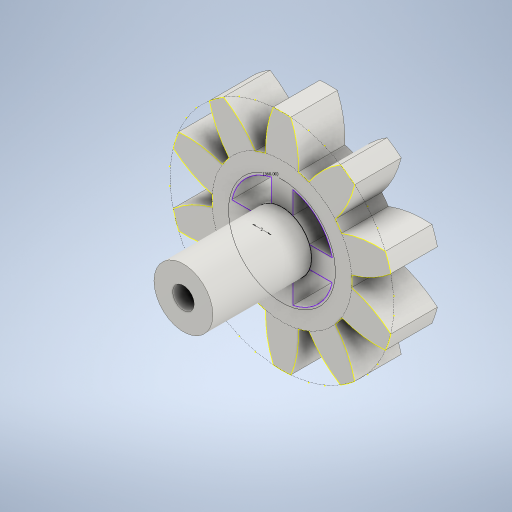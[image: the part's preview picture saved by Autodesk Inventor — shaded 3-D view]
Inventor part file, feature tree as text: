
AUTODESK INVENTOR PART (.ipt)
format: ipt  version: 2023 (Build 270158000, 158)  size: 431,104 bytes
history: native  units: mm (DEFAULTED — no unit token found)
features: extrude x4, sketch x3, plane x3, other x3, projected_geometry x1
ambient origin geometry x8: Origin, YZ Plane, XZ Plane, XY Plane, X Axis, Y Axis, Z Axis, Center Point
bodies: Solid1 (feature_tree)
feature tree (14):
  sketch  "Sketch1"  dims[d0=24.0mm d1=5.0mm d2=0.0mm]
  extrude  "Extrusion1"  Depth=5.0mm TaperAngle=0.0deg
  plane  "Work Plane2"
  plane  "Work Plane8"
  plane  "Work Plane9"
  other  "Spur Gear"
  extrude  "Extrusion2"  Depth=10.0mm TaperAngle=0.0deg
  sketch  "Sketch4"  dims[d16=40.0mm d17=0.0mm d34=3.141593mm d39=0.0mm d41=0.0mm d43=40.0mm d46=40.0mm d47=0.0mm d48=0.0mm d49=2.32mm d50=5.0mm d51=0.0mm d53=2.0mm d62=2.0mm d63=2.0mm d64=40.0mm d66=360.0deg d68=0.0mm d69=0.0mm d70=10.56mm d71=0.0mm]
  extrude  "Extrusion5"  Depth=10.56mm TaperAngle=0.0deg
  extrude  "Extrusion6"  TaperAngle=0.0deg  [1 undecoded]
  sketch  "Sketch2"  dims[d3=20.0mm d4=10.0mm d5=0.0mm]
  other  "Srf1"
  projected_geometry  "Projected Loop2"
  other  "Pitch Diameter"
note: 1 required parameter value undecoded (feature->parameter linkage not recoverable at this tier; creation-order binding heuristic only, values carry confidence <= 0.55)
